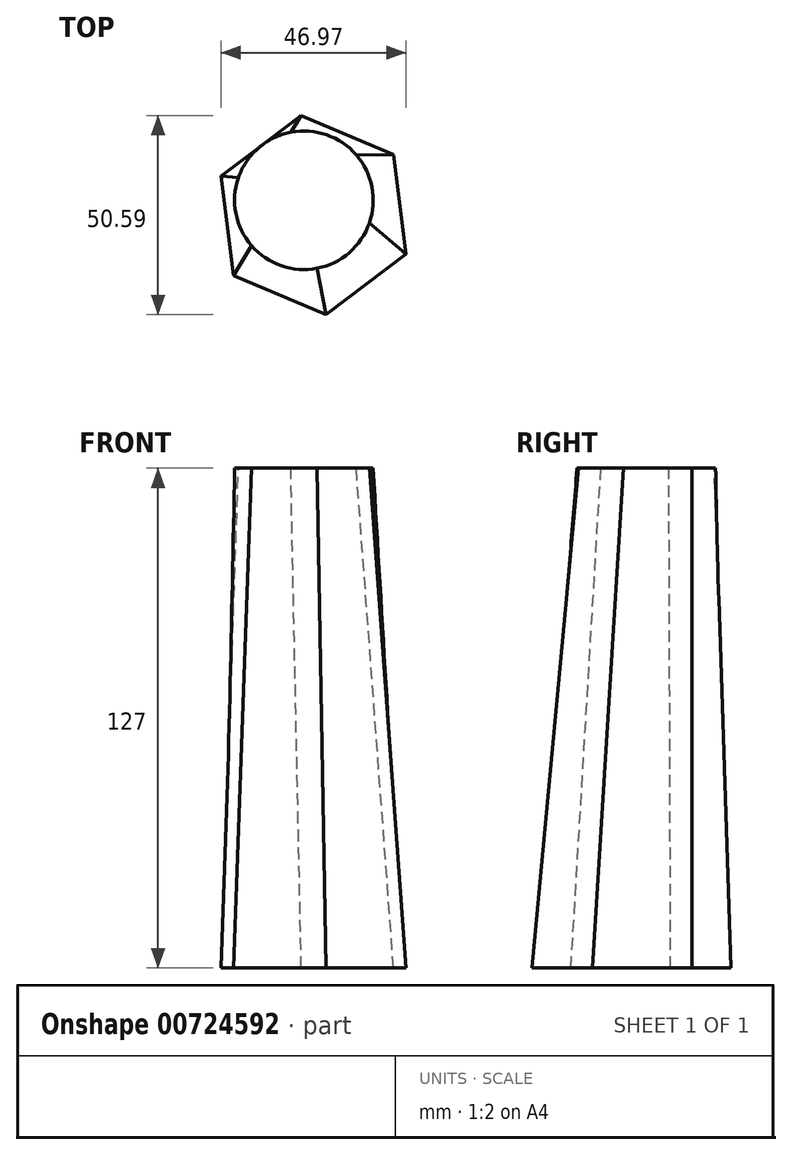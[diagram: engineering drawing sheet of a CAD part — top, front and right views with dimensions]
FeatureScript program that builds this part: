
annotation { "Feature Type Name" : "Feature", "Feature Type Description" : "" }
export const myFeature = defineFeature(function(context is Context, id is Id, definition is map)
    precondition{}
    {
        {
            var Q0;
            Q0=qCreatedBy(makeId("Top.planeOp"),FACE);
            cPlane(context, id + "F0", {"entities" : qUnion([Q0]), "cplaneType" : CPlaneType.OFFSET, "offset" : 127 * mm, "width" : 152.4 * mm, "height" : 152.4 * mm});
        }
        {
            var Q0;
            Q0=qCreatedBy(id+"F0.planeOp",FACE);
            var sketch = newSketch(context, id + "F1", { "sketchPlane" : qUnion([Q0])});
            skCircle(sketch, "E0", {"center": v(-38.57, 30.6) * mm, "radius": 17.6 * mm});
            skSolve(sketch);
        }
        {
            var Q0;
            Q0=qCreatedBy(makeId("Top.planeOp"),FACE);
            var sketch = newSketch(context, id + "F2", { "sketchPlane" : qUnion([Q0])});
            skCircle(sketch, "E1.cCircle", {"center": v(-36.11, 26.85) * mm, "radius": 22.08 * mm, "construction": true});
            skLineSegment(sketch, "E1.0", {"start": v(-32.96, 1.55) * mm, "end": v(-56.45, 11.47) * mm});
            skLineSegment(sketch, "E1.1", {"start": v(-56.45, 11.47) * mm, "end": v(-59.6, 36.77) * mm});
            skLineSegment(sketch, "E1.2", {"start": v(-59.6, 36.77) * mm, "end": v(-39.27, 52.14) * mm});
            skLineSegment(sketch, "E1.3", {"start": v(-39.27, 52.14) * mm, "end": v(-15.78, 42.22) * mm});
            skLineSegment(sketch, "E1.4", {"start": v(-15.78, 42.22) * mm, "end": v(-12.63, 16.93) * mm});
            skLineSegment(sketch, "E1.5", {"start": v(-12.63, 16.93) * mm, "end": v(-32.96, 1.55) * mm});
            skPoint(sketch, "E1.0.midPoint", {"position": v(-44.7, 6.51) * mm});
            skSolve(sketch);
        }
        {
            var Q0;
            Q0=makeQuery(id+"F2.imprint","IMPRINT",FACE,{"disambiguationData":[TD([[makeQuery(id+"F2.imprint","IMPRINT",EDGE,{"derivedFrom":sQuery(id+"F2.wireOp",EDGE,"E1.0")}),-1.0]])]});
            var Q1;
            Q1=makeQuery(id+"F1.imprint","IMPRINT",FACE,{"disambiguationData":[TD([[makeQuery(id+"F1.imprint","IMPRINT",EDGE,{"derivedFrom":sQuery(id+"F1.wireOp",EDGE,"E0")}),1.0]])]});
            loft(context, id + "F3", {"sheetProfilesArray" : [{ "sheetProfileEntities" : qUnion([Q0]) }, { "sheetProfileEntities" : qUnion([Q1]) }]});
        }
    });
